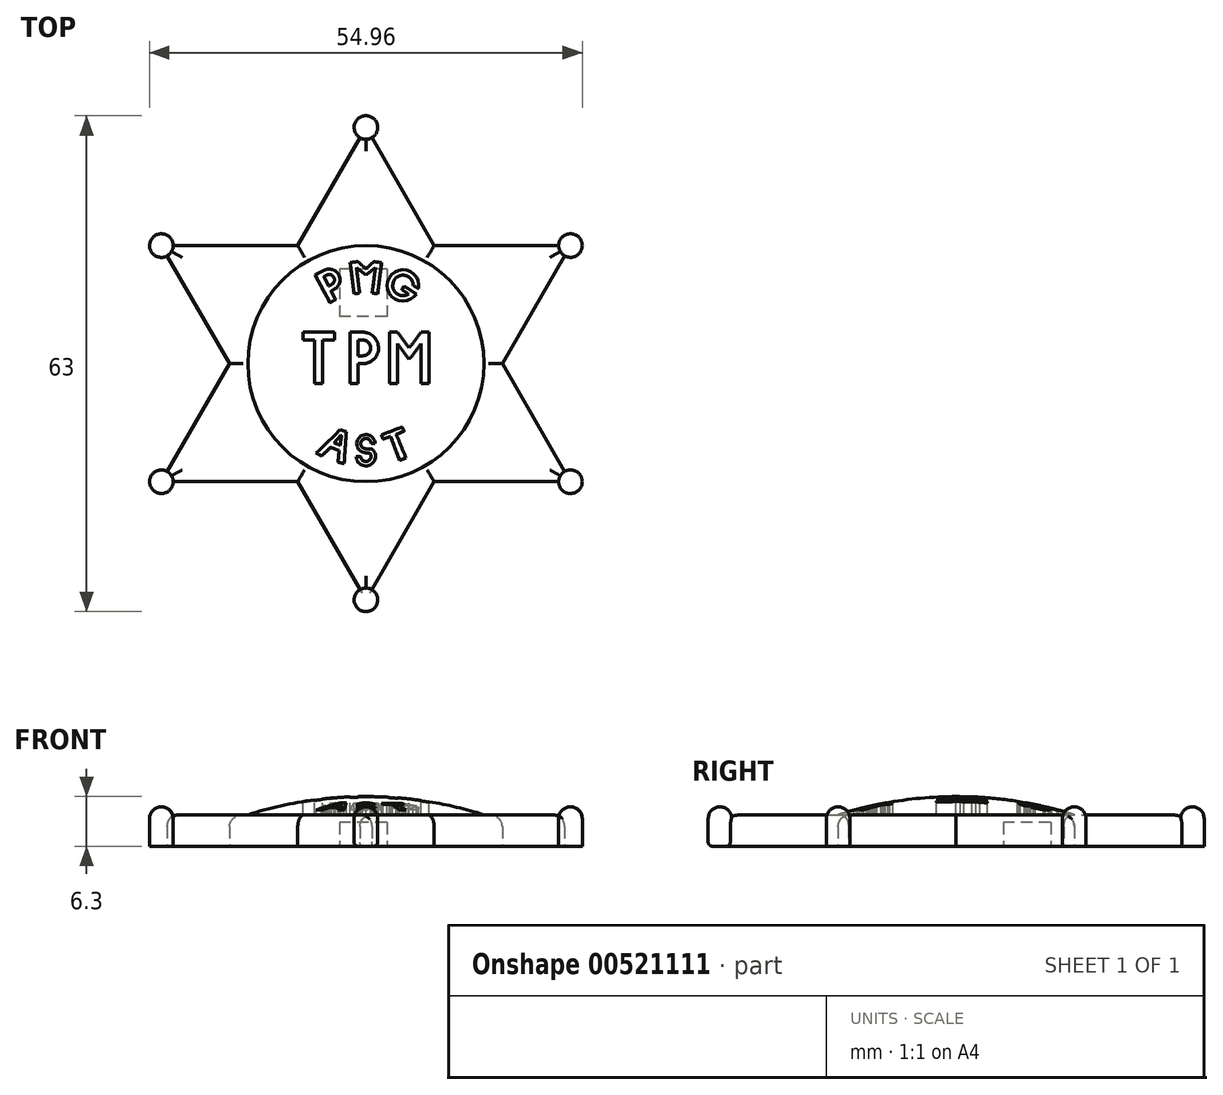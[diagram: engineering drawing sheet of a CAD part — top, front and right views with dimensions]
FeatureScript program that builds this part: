
annotation { "Feature Type Name" : "Feature", "Feature Type Description" : "" }
export const myFeature = defineFeature(function(context is Context, id is Id, definition is map)
    precondition{}
    {
        {
            var Q0;
            Q0=qCreatedBy(makeId("Top.planeOp"),FACE);
            var sketch = newSketch(context, id + "F0", { "sketchPlane" : qUnion([Q0])});
            skLineSegment(sketch, "E0", {"start": v(0, 30) * mm, "end": v(-8.66, 15) * mm});
            skLineSegment(sketch, "E1", {"start": v(-25.98, -15) * mm, "end": v(-8.66, -15) * mm});
            skLineSegment(sketch, "E2", {"start": v(25.98, -15) * mm, "end": v(17.32, 0) * mm});
            skLineSegment(sketch, "E3", {"start": v(-25.98, 15) * mm, "end": v(-17.32, 0) * mm});
            skLineSegment(sketch, "E4", {"start": v(0, -30) * mm, "end": v(8.66, -15) * mm});
            skLineSegment(sketch, "E5", {"start": v(25.98, 15) * mm, "end": v(8.66, 15) * mm});
            skLineSegment(sketch, "E6.trimOffspring", {"start": v(-8.66, -15) * mm, "end": v(0, -30) * mm});
            skLineSegment(sketch, "E7.trimOffspring", {"start": v(8.66, -15) * mm, "end": v(25.98, -15) * mm});
            skLineSegment(sketch, "E8.trimOffspring", {"start": v(-8.66, 15) * mm, "end": v(-25.98, 15) * mm});
            skLineSegment(sketch, "E9.trimOffspring", {"start": v(-17.32, 0) * mm, "end": v(-25.98, -15) * mm});
            skLineSegment(sketch, "E10.trimOffspring", {"start": v(17.32, 0) * mm, "end": v(25.98, 15) * mm});
            skLineSegment(sketch, "E11.trimOffspring", {"start": v(8.66, 15) * mm, "end": v(0, 30) * mm});
            skSolve(sketch);
        }
        {
            var Q0;
            Q0 = qSketchRegion(id + "F0", true);
            extrude(context, id + "F1", {"entities" : qUnion([Q0]), "depth" : 4 * mm, "offsetDistance" : 25 * mm});
        }
        {
            var Q0;
            Q0=qCreatedBy(makeId("Top.planeOp"),FACE);
            var sketch = newSketch(context, id + "F2", { "sketchPlane" : qUnion([Q0])});
            skCircle(sketch, "E12", {"center": v(0, 30) * mm, "radius": 1.5 * mm});
            skCircle(sketch, "E13", {"center": v(-25.98, 15) * mm, "radius": 1.5 * mm});
            skCircle(sketch, "E14", {"center": v(-25.98, -15) * mm, "radius": 1.5 * mm});
            skCircle(sketch, "E15", {"center": v(0, -30) * mm, "radius": 1.5 * mm});
            skCircle(sketch, "E16", {"center": v(25.98, -15) * mm, "radius": 1.5 * mm});
            skCircle(sketch, "E17", {"center": v(25.98, 15) * mm, "radius": 1.5 * mm});
            skSolve(sketch);
        }
        {
            var Q0;
            Q0 = qSketchRegion(id + "F2", true);
            extrude(context, id + "F3", {"entities" : qUnion([Q0]), "operationType" : NewBodyOperationType.ADD, "depth" : 5 * mm, "offsetDistance" : 25 * mm});
        }
        {
            var Q0;
            Q0=makeQuery(id+"F3.opExtrude","CAP_EDGE",EDGE,{"disambiguationData":[OSD([sQuery(id+"F2.wireOp",EDGE,"E15")])],"isStart":false});
            var Q1;
            Q1=makeQuery(id+"F3.opExtrude","CAP_EDGE",EDGE,{"disambiguationData":[OSD([sQuery(id+"F2.wireOp",EDGE,"E16")])],"isStart":false});
            var Q2;
            Q2=makeQuery(id+"F3.opExtrude","CAP_EDGE",EDGE,{"disambiguationData":[OSD([sQuery(id+"F2.wireOp",EDGE,"E17")])],"isStart":false});
            var Q3;
            Q3=makeQuery(id+"F3.opExtrude","CAP_EDGE",EDGE,{"disambiguationData":[OSD([sQuery(id+"F2.wireOp",EDGE,"E12")])],"isStart":false});
            var Q4;
            Q4=makeQuery(id+"F3.opExtrude","CAP_EDGE",EDGE,{"disambiguationData":[OSD([sQuery(id+"F2.wireOp",EDGE,"E13")])],"isStart":false});
            var Q5;
            Q5=makeQuery(id+"F3.opExtrude","CAP_EDGE",EDGE,{"disambiguationData":[OSD([sQuery(id+"F2.wireOp",EDGE,"E14")])],"isStart":false});
            fillet(context, id + "F4", {"entities" : qUnion([Q0, Q1, Q2, Q3, Q4, Q5]), "radius" : 1.5 * mm, "tangentPropagation" : true, "allowEdgeOverflow" : false});
        }
        {
            var Q0;
            Q0=makeQuery(id+"F1.opExtrude","CAP_EDGE",EDGE,{"disambiguationData":[OSD([sQuery(id+"F0.wireOp",EDGE,"E2")])],"isStart":false});
            var Q1;
            Q1=makeQuery(id+"F1.opExtrude","CAP_EDGE",EDGE,{"disambiguationData":[OSD([sQuery(id+"F0.wireOp",EDGE,"E10.trimOffspring")])],"isStart":false});
            var Q2;
            Q2=makeQuery(id+"F1.opExtrude","CAP_EDGE",EDGE,{"disambiguationData":[OSD([sQuery(id+"F0.wireOp",EDGE,"E5")])],"isStart":false});
            var Q3;
            Q3=makeQuery(id+"F1.opExtrude","CAP_EDGE",EDGE,{"disambiguationData":[OSD([sQuery(id+"F0.wireOp",EDGE,"E11.trimOffspring")])],"isStart":false});
            var Q4;
            Q4=makeQuery(id+"F1.opExtrude","CAP_EDGE",EDGE,{"disambiguationData":[OSD([sQuery(id+"F0.wireOp",EDGE,"E0")])],"isStart":false});
            var Q5;
            Q5=makeQuery(id+"F1.opExtrude","CAP_EDGE",EDGE,{"disambiguationData":[OSD([sQuery(id+"F0.wireOp",EDGE,"E8.trimOffspring")])],"isStart":false});
            var Q6;
            Q6=makeQuery(id+"F1.opExtrude","CAP_EDGE",EDGE,{"disambiguationData":[OSD([sQuery(id+"F0.wireOp",EDGE,"E3")])],"isStart":false});
            var Q7;
            Q7=makeQuery(id+"F1.opExtrude","CAP_EDGE",EDGE,{"disambiguationData":[OSD([sQuery(id+"F0.wireOp",EDGE,"E9.trimOffspring")])],"isStart":false});
            var Q8;
            Q8=makeQuery(id+"F1.opExtrude","CAP_EDGE",EDGE,{"disambiguationData":[OSD([sQuery(id+"F0.wireOp",EDGE,"E1")])],"isStart":false});
            var Q9;
            Q9=makeQuery(id+"F1.opExtrude","CAP_EDGE",EDGE,{"disambiguationData":[OSD([sQuery(id+"F0.wireOp",EDGE,"E6.trimOffspring")])],"isStart":false});
            var Q10;
            Q10=makeQuery(id+"F1.opExtrude","CAP_EDGE",EDGE,{"disambiguationData":[OSD([sQuery(id+"F0.wireOp",EDGE,"E4")])],"isStart":false});
            var Q11;
            Q11=makeQuery(id+"F1.opExtrude","CAP_EDGE",EDGE,{"disambiguationData":[OSD([sQuery(id+"F0.wireOp",EDGE,"E7.trimOffspring")])],"isStart":false});
            fillet(context, id + "F5", {"entities" : qUnion([Q0, Q1, Q2, Q3, Q4, Q5, Q6, Q7, Q8, Q9, Q10, Q11]), "radius" : 1.5 * mm, "tangentPropagation" : true, "allowEdgeOverflow" : false});
        }
        {
            var Q0;
            Q0=qCreatedBy(makeId("Right.planeOp"),FACE);
            var sketch = newSketch(context, id + "F6", { "sketchPlane" : qUnion([Q0])});
            skArc(sketch, "E18", {"start": v(15, 4) * mm, "mid": v(7.59, 5.72) * mm, "end": v(0, 6.3) * mm});
            skLineSegment(sketch, "E19", {"start": v(0, 4) * mm, "end": v(15, 4) * mm});
            skLineSegment(sketch, "E20", {"start": v(0, 4) * mm, "end": v(0, 6.3) * mm});
            skSolve(sketch);
        }
        {
            var Q0;
            Q0=qCreatedBy(makeId("Right.planeOp"),FACE);
            var sketch = newSketch(context, id + "F7", { "sketchPlane" : qUnion([Q0])});
            skLineSegment(sketch, "E21", {"start": v(0, 0) * mm, "end": v(0, 11.82) * mm});
            skSolve(sketch);
        }
        {
            var Q0;
            Q0 = qSketchRegion(id + "F6", true);
            var Q1;
            Q1=sQuery(id+"F7.wireOp",EDGE,"E21");
            revolve(context, id + "F8", {"operationType" : NewBodyOperationType.ADD, "entities" : qUnion([Q0]), "axis" : qUnion([Q1]), "revolveType" : RevolveType.FULL});
        }
        {
            var Q0;
            Q0=qCreatedBy(makeId("Top.planeOp"),FACE);
            cPlane(context, id + "F9", {"entities" : qUnion([Q0]), "cplaneType" : CPlaneType.OFFSET, "offset" : 7 * mm, "width" : 150 * mm, "height" : 150 * mm});
        }
        {
            var Q0;
            Q0=qCreatedBy(id+"F9.planeOp",FACE);
            var sketch = newSketch(context, id + "F10", { "sketchPlane" : qUnion([Q0])});
            skLineSegment(sketch, "E22", {"start": v(-6.5, 3) * mm, "end": v(-6.5, -2.5) * mm});
            skLineSegment(sketch, "E23", {"start": v(-6.5, -2.5) * mm, "end": v(-5.5, -2.5) * mm});
            skLineSegment(sketch, "E24", {"start": v(-5.5, -2.5) * mm, "end": v(-5.5, 3) * mm});
            skLineSegment(sketch, "E25", {"start": v(-5.5, 3) * mm, "end": v(-4, 3) * mm});
            skLineSegment(sketch, "E26", {"start": v(-4, 3) * mm, "end": v(-4, 4) * mm});
            skLineSegment(sketch, "E27", {"start": v(-4, 4) * mm, "end": v(-8, 4) * mm});
            skLineSegment(sketch, "E28", {"start": v(-8, 4) * mm, "end": v(-8, 3) * mm});
            skLineSegment(sketch, "E29", {"start": v(-8, 3) * mm, "end": v(-6.5, 3) * mm});
            skLineSegment(sketch, "E30", {"start": v(-2, -2.5) * mm, "end": v(-2, 4) * mm});
            skLineSegment(sketch, "E31", {"start": v(-2, -2.5) * mm, "end": v(-1, -2.5) * mm});
            skLineSegment(sketch, "E32", {"start": v(-1, -2.5) * mm, "end": v(-1, 0) * mm});
            skLineSegment(sketch, "E33", {"start": v(-1, 3) * mm, "end": v(-1, 1) * mm});
            skLineSegment(sketch, "E34", {"start": v(3, -2.5) * mm, "end": v(3, 4) * mm});
            skLineSegment(sketch, "E35", {"start": v(3, 4) * mm, "end": v(4, 4) * mm});
            skLineSegment(sketch, "E36", {"start": v(4, 4) * mm, "end": v(5.5, 2) * mm});
            skLineSegment(sketch, "E37", {"start": v(5.5, 2) * mm, "end": v(7, 4) * mm});
            skLineSegment(sketch, "E38", {"start": v(7, 4) * mm, "end": v(8, 4) * mm});
            skLineSegment(sketch, "E39", {"start": v(8, 4) * mm, "end": v(8, -2.5) * mm});
            skLineSegment(sketch, "E40", {"start": v(8, -2.5) * mm, "end": v(7, -2.5) * mm});
            skLineSegment(sketch, "E41", {"start": v(7, -2.5) * mm, "end": v(7, 2.54) * mm});
            skLineSegment(sketch, "E42", {"start": v(7, 2.54) * mm, "end": v(5.5, 0.54) * mm});
            skLineSegment(sketch, "E43", {"start": v(5.5, 0.54) * mm, "end": v(4, 2.54) * mm});
            skLineSegment(sketch, "E44", {"start": v(4, 2.54) * mm, "end": v(4, -2.5) * mm});
            skLineSegment(sketch, "E45", {"start": v(4, -2.5) * mm, "end": v(3, -2.5) * mm});
            skLineSegment(sketch, "E46", {"start": v(-1, 4) * mm, "end": v(-2, 4) * mm});
            skLineSegment(sketch, "E47", {"start": v(-1.5, 8.87) * mm, "end": v(-2, 12.85) * mm});
            skLineSegment(sketch, "E48", {"start": v(-2, 12.85) * mm, "end": v(-1.01, 12.96) * mm});
            skLineSegment(sketch, "E49", {"start": v(-1.01, 12.96) * mm, "end": v(0, 12.06) * mm});
            skLineSegment(sketch, "E50", {"start": v(0, 12.06) * mm, "end": v(1.01, 12.96) * mm});
            skLineSegment(sketch, "E51", {"start": v(1.01, 12.96) * mm, "end": v(2, 12.85) * mm});
            skLineSegment(sketch, "E52", {"start": v(2, 12.85) * mm, "end": v(1.5, 8.87) * mm});
            skLineSegment(sketch, "E53", {"start": v(1.5, 8.87) * mm, "end": v(0.8, 8.96) * mm});
            skLineSegment(sketch, "E54", {"start": v(0.8, 8.96) * mm, "end": v(1.2, 12.18) * mm});
            skLineSegment(sketch, "E55", {"start": v(1.2, 12.18) * mm, "end": v(0, 11.27) * mm});
            skLineSegment(sketch, "E56", {"start": v(0, 11.27) * mm, "end": v(-1.2, 12.18) * mm});
            skLineSegment(sketch, "E57", {"start": v(-1.2, 12.18) * mm, "end": v(-0.8, 8.96) * mm});
            skLineSegment(sketch, "E58", {"start": v(-0.8, 8.96) * mm, "end": v(-1.5, 8.87) * mm});
            skArc(sketch, "E59", {"start": v(6.66, 9.52) * mm, "mid": v(2.86, 10.7) * mm, "end": v(6.4, 8.87) * mm});
            skArc(sketch, "E60", {"start": v(6, 9.94) * mm, "mid": v(3.57, 10.56) * mm, "end": v(5.42, 8.85) * mm});
            skLineSegment(sketch, "E61", {"start": v(4.87, 9.84) * mm, "end": v(6.4, 8.87) * mm});
            skLineSegment(sketch, "E62", {"start": v(4.58, 9.39) * mm, "end": v(5.42, 8.85) * mm});
            skLineSegment(sketch, "E63", {"start": v(6, 9.94) * mm, "end": v(6.66, 9.52) * mm});
            skLineSegment(sketch, "E64", {"start": v(-4.57, 7.75) * mm, "end": v(-6.46, 11.28) * mm});
            skLineSegment(sketch, "E65", {"start": v(-6.46, 11.28) * mm, "end": v(-5.66, 11.7) * mm});
            skLineSegment(sketch, "E66", {"start": v(-5.34, 11.07) * mm, "end": v(-4.74, 9.86) * mm});
            skLineSegment(sketch, "E67", {"start": v(-3.87, 8.13) * mm, "end": v(-4.57, 7.75) * mm});
            skArc(sketch, "E68", {"start": v(-4.38, 10.04) * mm, "mid": v(-4.07, 10.97) * mm, "end": v(-5.01, 11.23) * mm});
            skArc(sketch, "E69", {"start": v(-4.07, 9.42) * mm, "mid": v(-3.43, 11.25) * mm, "end": v(-5.26, 11.89) * mm});
            skLineSegment(sketch, "E70", {"start": v(-4.38, 10.04) * mm, "end": v(-4.74, 9.86) * mm});
            skLineSegment(sketch, "E71", {"start": v(-4.04, 9.43) * mm, "end": v(-4.43, 9.24) * mm});
            skLineSegment(sketch, "E72", {"start": v(-5.66, 11.7) * mm, "end": v(-5.22, 11.9) * mm});
            skLineSegment(sketch, "E73", {"start": v(-4.93, 11.28) * mm, "end": v(-5.34, 11.07) * mm});
            skLineSegment(sketch, "E74.trimOffspring", {"start": v(-4.43, 9.24) * mm, "end": v(-3.87, 8.13) * mm});
            skLineSegment(sketch, "E75", {"start": v(4.58, 9.39) * mm, "end": v(4.87, 9.84) * mm});
            skLineSegment(sketch, "E76", {"start": v(-1, 4) * mm, "end": v(-0.4, 4) * mm});
            skLineSegment(sketch, "E77", {"start": v(-1, 3) * mm, "end": v(-0.4, 3) * mm});
            skLineSegment(sketch, "E78", {"start": v(-1, 1) * mm, "end": v(-0.4, 1) * mm});
            skLineSegment(sketch, "E79", {"start": v(-1, 0) * mm, "end": v(-0.4, 0) * mm});
            skArc(sketch, "E80", {"start": v(-0.4, 1) * mm, "mid": v(0.6, 2) * mm, "end": v(-0.4, 3) * mm});
            skArc(sketch, "E81", {"start": v(-0.4, 0) * mm, "mid": v(1.6, 2) * mm, "end": v(-0.4, 4) * mm});
            skLineSegment(sketch, "E82", {"start": v(-6.3, -11.37) * mm, "end": v(-3.26, -8.39) * mm});
            skLineSegment(sketch, "E83", {"start": v(-3.26, -8.39) * mm, "end": v(-2.49, -8.65) * mm});
            skLineSegment(sketch, "E84", {"start": v(-2.49, -8.65) * mm, "end": v(-2.77, -12.7) * mm});
            skLineSegment(sketch, "E85", {"start": v(-2.77, -12.7) * mm, "end": v(-3.55, -12.5) * mm});
            skLineSegment(sketch, "E86", {"start": v(-3.55, -12.5) * mm, "end": v(-3.39, -11.05) * mm});
            skLineSegment(sketch, "E87", {"start": v(-3.39, -11.05) * mm, "end": v(-4.5, -10.62) * mm});
            skLineSegment(sketch, "E88", {"start": v(-4.5, -10.62) * mm, "end": v(-5.6, -11.73) * mm});
            skLineSegment(sketch, "E89", {"start": v(-4.03, -10.07) * mm, "end": v(-3.21, -9.1) * mm});
            skLineSegment(sketch, "E90", {"start": v(-3.21, -9.1) * mm, "end": v(-3.1, -9.15) * mm});
            skLineSegment(sketch, "E91", {"start": v(-3.1, -9.15) * mm, "end": v(-3.26, -10.36) * mm});
            skLineSegment(sketch, "E92", {"start": v(-3.26, -10.36) * mm, "end": v(-4.03, -10.07) * mm});
            skLineSegment(sketch, "E93", {"start": v(4.59, -8.05) * mm, "end": v(2, -9.04) * mm});
            skLineSegment(sketch, "E94", {"start": v(2, -9.04) * mm, "end": v(2.17, -9.58) * mm});
            skLineSegment(sketch, "E95", {"start": v(2.17, -9.58) * mm, "end": v(3.15, -9.25) * mm});
            skLineSegment(sketch, "E96", {"start": v(3.15, -9.25) * mm, "end": v(4.3, -12.27) * mm});
            skLineSegment(sketch, "E97", {"start": v(4.3, -12.27) * mm, "end": v(5.11, -11.95) * mm});
            skLineSegment(sketch, "E98", {"start": v(5.11, -11.95) * mm, "end": v(3.85, -9.02) * mm});
            skLineSegment(sketch, "E99", {"start": v(3.85, -9.02) * mm, "end": v(4.86, -8.59) * mm});
            skLineSegment(sketch, "E100", {"start": v(4.86, -8.59) * mm, "end": v(4.59, -8.05) * mm});
            skArc(sketch, "E101", {"start": v(1.16, -10.16) * mm, "mid": v(-0.58, -9.15) * mm, "end": v(-0.6, -11.16) * mm});
            skArc(sketch, "E102", {"start": v(0.66, -10.16) * mm, "mid": v(-0.3, -9.57) * mm, "end": v(-0.4, -10.7) * mm});
            skLineSegment(sketch, "E103", {"start": v(0.66, -10.16) * mm, "end": v(1.16, -10.16) * mm});
            skArc(sketch, "E104", {"start": v(-0.65, -11.77) * mm, "mid": v(0.11, -12.42) * mm, "end": v(0.62, -11.55) * mm});
            skLineSegment(sketch, "E105", {"start": v(-0.65, -11.77) * mm, "end": v(-1.23, -11.77) * mm});
            skArc(sketch, "E106.trimOffspring", {"start": v(-1.23, -11.77) * mm, "mid": v(0.43, -12.92) * mm, "end": v(0.93, -10.97) * mm});
            skArc(sketch, "E107", {"start": v(-0.6, -11.16) * mm, "mid": v(-0.13, -11.3) * mm, "end": v(0.34, -11.35) * mm});
            skArc(sketch, "E108", {"start": v(-0.4, -10.7) * mm, "mid": v(0.09, -10.82) * mm, "end": v(0.6, -10.84) * mm});
            skArc(sketch, "E109", {"start": v(0.62, -11.55) * mm, "mid": v(0.5, -11.41) * mm, "end": v(0.34, -11.35) * mm});
            skArc(sketch, "E110", {"start": v(0.93, -10.97) * mm, "mid": v(0.78, -10.86) * mm, "end": v(0.6, -10.84) * mm});
            skLineSegment(sketch, "E111", {"start": v(-6.3, -11.37) * mm, "end": v(-5.6, -11.73) * mm});
            skSolve(sketch);
        }
        {
            var Q0;
            Q0 = qSketchRegion(id + "F10", true);
            extrude(context, id + "F11", {"entities" : qUnion([Q0]), "operationType" : NewBodyOperationType.REMOVE, "oppositeDirection" : true, "depth" : 3 * mm, "offsetDistance" : 25 * mm});
        }
        {
            var Q0;
            Q0=qCreatedBy(makeId("Top.planeOp"),FACE);
            var sketch = newSketch(context, id + "F12", { "sketchPlane" : qUnion([Q0])});
            skLineSegment(sketch, "E112.bottom", {"start": v(2.66, 12) * mm, "end": v(-3.34, 12) * mm});
            skLineSegment(sketch, "E112.top", {"start": v(2.66, 6) * mm, "end": v(-3.34, 6) * mm});
            skLineSegment(sketch, "E112.left", {"start": v(2.66, 12) * mm, "end": v(2.66, 6) * mm});
            skLineSegment(sketch, "E112.right", {"start": v(-3.34, 12) * mm, "end": v(-3.34, 6) * mm});
            skSolve(sketch);
        }
        {
            var Q0;
            Q0 = qSketchRegion(id + "F12", true);
            extrude(context, id + "F13", {"entities" : qUnion([Q0]), "operationType" : NewBodyOperationType.REMOVE, "depth" : 3 * mm, "offsetDistance" : 25 * mm});
        }
        {
            var Q0;
            Q0=makeQuery(id+"F3.opExtrude","CAP_EDGE",EDGE,{"disambiguationData":[OSD([sQuery(id+"F2.wireOp",EDGE,"E15")])],"isStart":true});
            fillet(context, id + "F14", {"entities" : qUnion([Q0]), "radius" : 0.5 * mm, "tangentPropagation" : true, "allowEdgeOverflow" : false});
        }
    });
